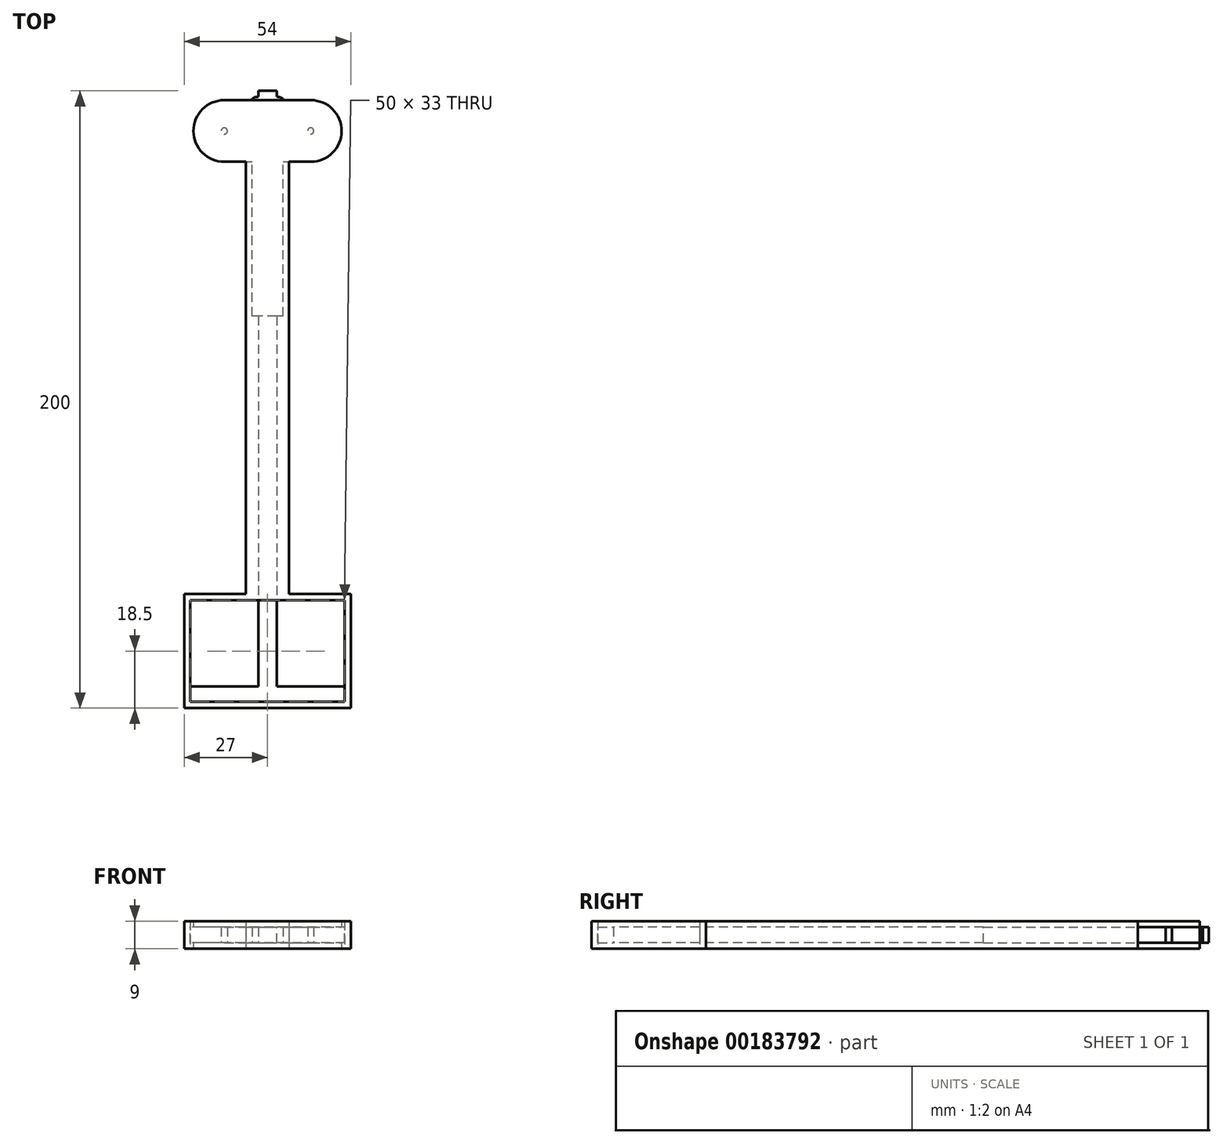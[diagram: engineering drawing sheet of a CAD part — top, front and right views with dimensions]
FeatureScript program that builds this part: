
annotation { "Feature Type Name" : "Feature", "Feature Type Description" : "" }
export const myFeature = defineFeature(function(context is Context, id is Id, definition is map)
    precondition{}
    {
        {
            var Q0;
            Q0=qCreatedBy(makeId("Top.planeOp"),FACE);
            var sketch = newSketch(context, id + "F0", { "sketchPlane" : qUnion([Q0])});
            skLineSegment(sketch, "E0.bottom", {"start": v(0, 13) * mm, "end": v(3, 13) * mm});
            skLineSegment(sketch, "E0.top", {"start": v(0, -180) * mm, "end": v(3, -180) * mm});
            skLineSegment(sketch, "E0.left", {"start": v(0, 13) * mm, "end": v(0, -180) * mm});
            skLineSegment(sketch, "E0.right", {"start": v(3, 13) * mm, "end": v(3, -180) * mm});
            skLineSegment(sketch, "E1", {"start": v(0, 10) * mm, "end": v(3, 10) * mm, "construction": true});
            skArc(sketch, "E2", {"start": v(3, 11.09) * mm, "mid": v(4.04, 10.94) * mm, "end": v(5, 10.5) * mm});
            skLineSegment(sketch, "E3", {"start": v(5, 10.5) * mm, "end": v(5, 10) * mm});
            skArc(sketch, "E4.MirrorCS", {"start": v(3, 8.91) * mm, "mid": v(4.04, 9.06) * mm, "end": v(5, 9.5) * mm});
            skLineSegment(sketch, "E5.MirrorCS", {"start": v(5, 9.5) * mm, "end": v(5, 10) * mm});
            skArc(sketch, "E6.1.0.0", {"start": v(3, 7.89) * mm, "mid": v(4.04, 7.74) * mm, "end": v(5, 7.3) * mm});
            skLineSegment(sketch, "E6.1.0.1", {"start": v(5, 7.3) * mm, "end": v(5, 6.8) * mm});
            skLineSegment(sketch, "E6.1.0.2", {"start": v(5, 6.3) * mm, "end": v(5, 6.8) * mm});
            skArc(sketch, "E6.1.0.3", {"start": v(3, 5.71) * mm, "mid": v(4.04, 5.86) * mm, "end": v(5, 6.3) * mm});
            skArc(sketch, "E6.2.0.0", {"start": v(3, 4.69) * mm, "mid": v(4.04, 4.54) * mm, "end": v(5, 4.1) * mm});
            skLineSegment(sketch, "E6.2.0.1", {"start": v(5, 4.1) * mm, "end": v(5, 3.6) * mm});
            skLineSegment(sketch, "E6.2.0.2", {"start": v(5, 3.1) * mm, "end": v(5, 3.6) * mm});
            skArc(sketch, "E6.2.0.3", {"start": v(3, 2.51) * mm, "mid": v(4.04, 2.66) * mm, "end": v(5, 3.1) * mm});
            skLineSegment(sketch, "E6.direction1", {"start": v(3, 7.39) * mm, "end": v(3, 4.19) * mm, "construction": true});
            skArc(sketch, "E7.0.3.0", {"start": v(3, 1.49) * mm, "mid": v(4.04, 1.34) * mm, "end": v(5, 0.9) * mm});
            skLineSegment(sketch, "E7.4.3.0", {"start": v(5, 0.9) * mm, "end": v(5, 0.4) * mm});
            skLineSegment(sketch, "E7.7.3.0", {"start": v(5, -0.1) * mm, "end": v(5, 0.4) * mm});
            skArc(sketch, "E7.10.3.0", {"start": v(3, -0.69) * mm, "mid": v(4.04, -0.54) * mm, "end": v(5, -0.1) * mm});
            skArc(sketch, "E7.0.4.0", {"start": v(3, -1.71) * mm, "mid": v(4.04, -1.86) * mm, "end": v(5, -2.3) * mm});
            skLineSegment(sketch, "E7.4.4.0", {"start": v(5, -2.3) * mm, "end": v(5, -2.8) * mm});
            skLineSegment(sketch, "E7.7.4.0", {"start": v(5, -3.3) * mm, "end": v(5, -2.8) * mm});
            skArc(sketch, "E7.10.4.0", {"start": v(3, -3.89) * mm, "mid": v(4.04, -3.74) * mm, "end": v(5, -3.3) * mm});
            skArc(sketch, "E7.0.5.0", {"start": v(3, -4.91) * mm, "mid": v(4.04, -5.06) * mm, "end": v(5, -5.5) * mm});
            skLineSegment(sketch, "E7.4.5.0", {"start": v(5, -5.5) * mm, "end": v(5, -6) * mm});
            skLineSegment(sketch, "E7.7.5.0", {"start": v(5, -6.5) * mm, "end": v(5, -6) * mm});
            skArc(sketch, "E7.10.5.0", {"start": v(3, -7.09) * mm, "mid": v(4.04, -6.94) * mm, "end": v(5, -6.5) * mm});
            skArc(sketch, "E7.0.6.0", {"start": v(3, -8.11) * mm, "mid": v(4.04, -8.26) * mm, "end": v(5, -8.7) * mm});
            skLineSegment(sketch, "E7.4.6.0", {"start": v(5, -8.7) * mm, "end": v(5, -9.2) * mm});
            skLineSegment(sketch, "E7.7.6.0", {"start": v(5, -9.7) * mm, "end": v(5, -9.2) * mm});
            skArc(sketch, "E7.10.6.0", {"start": v(3, -10.29) * mm, "mid": v(4.04, -10.14) * mm, "end": v(5, -9.7) * mm});
            skArc(sketch, "E7.0.7.0", {"start": v(3, -11.31) * mm, "mid": v(4.04, -11.46) * mm, "end": v(5, -11.9) * mm});
            skLineSegment(sketch, "E7.4.7.0", {"start": v(5, -11.9) * mm, "end": v(5, -12.4) * mm});
            skLineSegment(sketch, "E7.7.7.0", {"start": v(5, -12.9) * mm, "end": v(5, -12.4) * mm});
            skArc(sketch, "E7.10.7.0", {"start": v(3, -13.49) * mm, "mid": v(4.04, -13.34) * mm, "end": v(5, -12.9) * mm});
            skArc(sketch, "E7.0.8.0", {"start": v(3, -14.51) * mm, "mid": v(4.04, -14.66) * mm, "end": v(5, -15.1) * mm});
            skLineSegment(sketch, "E7.4.8.0", {"start": v(5, -15.1) * mm, "end": v(5, -15.6) * mm});
            skLineSegment(sketch, "E7.7.8.0", {"start": v(5, -16.1) * mm, "end": v(5, -15.6) * mm});
            skArc(sketch, "E7.10.8.0", {"start": v(3, -16.69) * mm, "mid": v(4.04, -16.54) * mm, "end": v(5, -16.1) * mm});
            skArc(sketch, "E7.0.9.0", {"start": v(3, -17.71) * mm, "mid": v(4.04, -17.86) * mm, "end": v(5, -18.3) * mm});
            skLineSegment(sketch, "E7.4.9.0", {"start": v(5, -18.3) * mm, "end": v(5, -18.8) * mm});
            skLineSegment(sketch, "E7.7.9.0", {"start": v(5, -19.3) * mm, "end": v(5, -18.8) * mm});
            skArc(sketch, "E7.10.9.0", {"start": v(3, -19.89) * mm, "mid": v(4.04, -19.74) * mm, "end": v(5, -19.3) * mm});
            skArc(sketch, "E7.0.10.0", {"start": v(3, -20.91) * mm, "mid": v(4.04, -21.06) * mm, "end": v(5, -21.5) * mm});
            skLineSegment(sketch, "E7.4.10.0", {"start": v(5, -21.5) * mm, "end": v(5, -22) * mm});
            skLineSegment(sketch, "E7.7.10.0", {"start": v(5, -22.5) * mm, "end": v(5, -22) * mm});
            skArc(sketch, "E7.10.10.0", {"start": v(3, -23.09) * mm, "mid": v(4.04, -22.94) * mm, "end": v(5, -22.5) * mm});
            skArc(sketch, "E7.0.11.0", {"start": v(3, -24.11) * mm, "mid": v(4.04, -24.26) * mm, "end": v(5, -24.7) * mm});
            skLineSegment(sketch, "E7.4.11.0", {"start": v(5, -24.7) * mm, "end": v(5, -25.2) * mm});
            skLineSegment(sketch, "E7.7.11.0", {"start": v(5, -25.7) * mm, "end": v(5, -25.2) * mm});
            skArc(sketch, "E7.10.11.0", {"start": v(3, -26.29) * mm, "mid": v(4.04, -26.14) * mm, "end": v(5, -25.7) * mm});
            skArc(sketch, "E7.0.12.0", {"start": v(3, -27.31) * mm, "mid": v(4.04, -27.46) * mm, "end": v(5, -27.9) * mm});
            skLineSegment(sketch, "E7.4.12.0", {"start": v(5, -27.9) * mm, "end": v(5, -28.4) * mm});
            skLineSegment(sketch, "E7.7.12.0", {"start": v(5, -28.9) * mm, "end": v(5, -28.4) * mm});
            skArc(sketch, "E7.10.12.0", {"start": v(3, -29.49) * mm, "mid": v(4.04, -29.34) * mm, "end": v(5, -28.9) * mm});
            skArc(sketch, "E7.0.13.0", {"start": v(3, -30.51) * mm, "mid": v(4.04, -30.66) * mm, "end": v(5, -31.1) * mm});
            skLineSegment(sketch, "E7.4.13.0", {"start": v(5, -31.1) * mm, "end": v(5, -31.6) * mm});
            skLineSegment(sketch, "E7.7.13.0", {"start": v(5, -32.1) * mm, "end": v(5, -31.6) * mm});
            skArc(sketch, "E7.10.13.0", {"start": v(3, -32.69) * mm, "mid": v(4.04, -32.54) * mm, "end": v(5, -32.1) * mm});
            skArc(sketch, "E7.0.14.0", {"start": v(3, -33.71) * mm, "mid": v(4.04, -33.86) * mm, "end": v(5, -34.3) * mm});
            skLineSegment(sketch, "E7.4.14.0", {"start": v(5, -34.3) * mm, "end": v(5, -34.8) * mm});
            skLineSegment(sketch, "E7.7.14.0", {"start": v(5, -35.3) * mm, "end": v(5, -34.8) * mm});
            skArc(sketch, "E7.10.14.0", {"start": v(3, -35.89) * mm, "mid": v(4.04, -35.74) * mm, "end": v(5, -35.3) * mm});
            skArc(sketch, "E7.0.15.0", {"start": v(3, -36.91) * mm, "mid": v(4.04, -37.06) * mm, "end": v(5, -37.5) * mm});
            skLineSegment(sketch, "E7.4.15.0", {"start": v(5, -37.5) * mm, "end": v(5, -38) * mm});
            skLineSegment(sketch, "E7.7.15.0", {"start": v(5, -38.5) * mm, "end": v(5, -38) * mm});
            skArc(sketch, "E7.10.15.0", {"start": v(3, -39.09) * mm, "mid": v(4.04, -38.94) * mm, "end": v(5, -38.5) * mm});
            skSolve(sketch);
        }
        {
            var Q0;
            Q0 = qSketchRegion(id + "F0", true);
            extrude(context, id + "F1", {"entities" : qUnion([Q0]), "depth" : 5 * mm});
        }
        {
            var Q0;
            Q0=makeQuery(id+"F1.opExtrude","SWEPT_BODY",BODY,{"disambiguationData":[OSD([sQuery(id+"F0.wireOp",EDGE,"E0.bottom"),sQuery(id+"F0.wireOp",EDGE,"E0.top"),sQuery(id+"F0.wireOp",EDGE,"E0.left"),sQuery(id+"F0.wireOp",EDGE,"E0.right"),sQuery(id+"F0.wireOp",EDGE,"E2"),sQuery(id+"F0.wireOp",EDGE,"E3"),sQuery(id+"F0.wireOp",EDGE,"E4.MirrorCS"),sQuery(id+"F0.wireOp",EDGE,"E5.MirrorCS"),sQuery(id+"F0.wireOp",EDGE,"E6.1.0.0"),sQuery(id+"F0.wireOp",EDGE,"E6.1.0.1"),sQuery(id+"F0.wireOp",EDGE,"E6.1.0.2"),sQuery(id+"F0.wireOp",EDGE,"E6.1.0.3"),sQuery(id+"F0.wireOp",EDGE,"E6.2.0.0"),sQuery(id+"F0.wireOp",EDGE,"E6.2.0.1"),sQuery(id+"F0.wireOp",EDGE,"E6.2.0.2"),sQuery(id+"F0.wireOp",EDGE,"E6.2.0.3"),sQuery(id+"F0.wireOp",EDGE,"E7.0.3.0"),sQuery(id+"F0.wireOp",EDGE,"E7.4.3.0"),sQuery(id+"F0.wireOp",EDGE,"E7.7.3.0"),sQuery(id+"F0.wireOp",EDGE,"E7.10.3.0"),sQuery(id+"F0.wireOp",EDGE,"E7.0.4.0"),sQuery(id+"F0.wireOp",EDGE,"E7.4.4.0"),sQuery(id+"F0.wireOp",EDGE,"E7.7.4.0"),sQuery(id+"F0.wireOp",EDGE,"E7.10.4.0"),sQuery(id+"F0.wireOp",EDGE,"E7.0.5.0"),sQuery(id+"F0.wireOp",EDGE,"E7.4.5.0"),sQuery(id+"F0.wireOp",EDGE,"E7.7.5.0"),sQuery(id+"F0.wireOp",EDGE,"E7.10.5.0"),sQuery(id+"F0.wireOp",EDGE,"E7.0.6.0"),sQuery(id+"F0.wireOp",EDGE,"E7.4.6.0"),sQuery(id+"F0.wireOp",EDGE,"E7.7.6.0"),sQuery(id+"F0.wireOp",EDGE,"E7.10.6.0"),sQuery(id+"F0.wireOp",EDGE,"E7.0.7.0"),sQuery(id+"F0.wireOp",EDGE,"E7.4.7.0"),sQuery(id+"F0.wireOp",EDGE,"E7.7.7.0"),sQuery(id+"F0.wireOp",EDGE,"E7.10.7.0"),sQuery(id+"F0.wireOp",EDGE,"E7.0.8.0"),sQuery(id+"F0.wireOp",EDGE,"E7.4.8.0"),sQuery(id+"F0.wireOp",EDGE,"E7.7.8.0"),sQuery(id+"F0.wireOp",EDGE,"E7.10.8.0"),sQuery(id+"F0.wireOp",EDGE,"E7.0.9.0"),sQuery(id+"F0.wireOp",EDGE,"E7.4.9.0"),sQuery(id+"F0.wireOp",EDGE,"E7.7.9.0"),sQuery(id+"F0.wireOp",EDGE,"E7.10.9.0"),sQuery(id+"F0.wireOp",EDGE,"E7.0.10.0"),sQuery(id+"F0.wireOp",EDGE,"E7.4.10.0"),sQuery(id+"F0.wireOp",EDGE,"E7.7.10.0"),sQuery(id+"F0.wireOp",EDGE,"E7.10.10.0"),sQuery(id+"F0.wireOp",EDGE,"E7.0.11.0"),sQuery(id+"F0.wireOp",EDGE,"E7.4.11.0"),sQuery(id+"F0.wireOp",EDGE,"E7.7.11.0"),sQuery(id+"F0.wireOp",EDGE,"E7.10.11.0"),sQuery(id+"F0.wireOp",EDGE,"E7.0.12.0"),sQuery(id+"F0.wireOp",EDGE,"E7.4.12.0"),sQuery(id+"F0.wireOp",EDGE,"E7.7.12.0"),sQuery(id+"F0.wireOp",EDGE,"E7.10.12.0"),sQuery(id+"F0.wireOp",EDGE,"E7.0.13.0"),sQuery(id+"F0.wireOp",EDGE,"E7.4.13.0"),sQuery(id+"F0.wireOp",EDGE,"E7.7.13.0"),sQuery(id+"F0.wireOp",EDGE,"E7.10.13.0"),sQuery(id+"F0.wireOp",EDGE,"E7.0.14.0"),sQuery(id+"F0.wireOp",EDGE,"E7.4.14.0"),sQuery(id+"F0.wireOp",EDGE,"E7.7.14.0"),sQuery(id+"F0.wireOp",EDGE,"E7.10.14.0"),sQuery(id+"F0.wireOp",EDGE,"E7.0.15.0"),sQuery(id+"F0.wireOp",EDGE,"E7.4.15.0"),sQuery(id+"F0.wireOp",EDGE,"E7.7.15.0"),sQuery(id+"F0.wireOp",EDGE,"E7.10.15.0")])]});
            var Q1;
            Q1=makeQuery(id+"F1.opExtrude","SWEPT_FACE",FACE,{"disambiguationData":[OSD([sQuery(id+"F0.wireOp",EDGE,"E0.left")])]});
            mirror(context, id + "F2", {"operationType" : NewBodyOperationType.ADD, "entities" : qUnion([Q0]), "mirrorPlane" : qUnion([Q1])});
        }
        {
            var Q0;
            {var subQ0=makeQuery(id+"F1.opExtrude","SWEPT_FACE",FACE,{"disambiguationData":[OSD([sQuery(id+"F0.wireOp",EDGE,"E0.top")])]});Q0=makeQuery(id+"F2.boolean.opBoolean","MERGE",FACE,{"derivedFrom":[subQ0,makeQuery(id+"F2.opPattern","COPY",FACE,{"derivedFrom":subQ0,"instanceName":"1"})]});}
            var sketch = newSketch(context, id + "F3", { "sketchPlane" : qUnion([Q0])});
            skLineSegment(sketch, "E8.bottom", {"start": v(25, 0) * mm, "end": v(-25, 0) * mm});
            skLineSegment(sketch, "E8.top", {"start": v(25, 5) * mm, "end": v(-25, 5) * mm});
            skLineSegment(sketch, "E8.left", {"start": v(25, 0) * mm, "end": v(25, 5) * mm});
            skLineSegment(sketch, "E8.right", {"start": v(-25, 0) * mm, "end": v(-25, 5) * mm});
            skPoint(sketch, "E8.middle", {"position": v(0, 2.5) * mm});
            skPoint(sketch, "E8.middle.positionSnap0", {"position": v(3, 2.5) * mm});
            skPoint(sketch, "E8.centerSnap0", {"position": v(3, 2.5) * mm});
            skSolve(sketch);
        }
        {
            var Q0;
            Q0 = qSketchRegion(id + "F3", true);
            extrude(context, id + "F4", {"entities" : qUnion([Q0]), "operationType" : NewBodyOperationType.ADD, "depth" : 5 * mm});
        }
        {
            var Q0;
            Q0=qCreatedBy(makeId("Top.planeOp"),FACE);
            var sketch = newSketch(context, id + "F5", { "sketchPlane" : qUnion([Q0])});
            skCircle(sketch, "E9", {"center": v(14, 0) * mm, "radius": 10 * mm});
            skLineSegment(sketch, "E10", {"start": v(0, 10) * mm, "end": v(14, 10) * mm});
            skLineSegment(sketch, "E11", {"start": v(14, -10) * mm, "end": v(7, -10) * mm});
            skLineSegment(sketch, "E12", {"start": v(7, -10) * mm, "end": v(7, -150) * mm});
            skLineSegment(sketch, "E13", {"start": v(7, -150) * mm, "end": v(27, -150) * mm});
            skLineSegment(sketch, "E14", {"start": v(27, -150) * mm, "end": v(27, -187) * mm});
            skLineSegment(sketch, "E15", {"start": v(27, -187) * mm, "end": v(0, -187) * mm});
            skLineSegment(sketch, "E16.MirrorCS", {"start": v(0, 10) * mm, "end": v(-14, 10) * mm});
            skCircle(sketch, "E17.MirrorC", {"center": v(-14, 0) * mm, "radius": 10 * mm});
            skLineSegment(sketch, "E18.MirrorCS", {"start": v(-14, -10) * mm, "end": v(-7, -10) * mm});
            skLineSegment(sketch, "E19.MirrorCS", {"start": v(-7, -10) * mm, "end": v(-7, -150) * mm});
            skLineSegment(sketch, "E20.MirrorCS", {"start": v(-7, -150) * mm, "end": v(-27, -150) * mm});
            skLineSegment(sketch, "E21.MirrorCS", {"start": v(-27, -150) * mm, "end": v(-27, -187) * mm});
            skLineSegment(sketch, "E22.MirrorCS", {"start": v(-27, -187) * mm, "end": v(0, -187) * mm});
            skLineSegment(sketch, "E23.bottom", {"start": v(-25, -185) * mm, "end": v(25, -185) * mm});
            skLineSegment(sketch, "E23.top", {"start": v(-25, -152) * mm, "end": v(25, -152) * mm});
            skLineSegment(sketch, "E23.left", {"start": v(-25, -185) * mm, "end": v(-25, -152) * mm});
            skLineSegment(sketch, "E23.right", {"start": v(25, -185) * mm, "end": v(25, -152) * mm});
            skPoint(sketch, "E23.middle", {"position": v(0, -168.5) * mm});
            skSolve(sketch);
        }
        {
            var Q0;
            Q0 = qSketchRegion(id + "F5", true);
            extrude(context, id + "F6", {"entities" : qUnion([Q0]), "depth" : 7 * mm, "hasSecondDirection" : true, "secondDirectionOppositeDirection" : true, "secondDirectionDepth" : 2 * mm});
        }
        {
            var Q0;
            Q0=makeQuery(id+"F1.opExtrude","SWEPT_BODY",BODY,{"disambiguationData":[OSD([sQuery(id+"F0.wireOp",EDGE,"E0.bottom"),sQuery(id+"F0.wireOp",EDGE,"E0.top"),sQuery(id+"F0.wireOp",EDGE,"E0.left"),sQuery(id+"F0.wireOp",EDGE,"E0.right"),sQuery(id+"F0.wireOp",EDGE,"E2"),sQuery(id+"F0.wireOp",EDGE,"E3"),sQuery(id+"F0.wireOp",EDGE,"E4.MirrorCS"),sQuery(id+"F0.wireOp",EDGE,"E5.MirrorCS"),sQuery(id+"F0.wireOp",EDGE,"E6.1.0.0"),sQuery(id+"F0.wireOp",EDGE,"E6.1.0.1"),sQuery(id+"F0.wireOp",EDGE,"E6.1.0.2"),sQuery(id+"F0.wireOp",EDGE,"E6.1.0.3"),sQuery(id+"F0.wireOp",EDGE,"E6.2.0.0"),sQuery(id+"F0.wireOp",EDGE,"E6.2.0.1"),sQuery(id+"F0.wireOp",EDGE,"E6.2.0.2"),sQuery(id+"F0.wireOp",EDGE,"E6.2.0.3"),sQuery(id+"F0.wireOp",EDGE,"E7.0.3.0"),sQuery(id+"F0.wireOp",EDGE,"E7.4.3.0"),sQuery(id+"F0.wireOp",EDGE,"E7.7.3.0"),sQuery(id+"F0.wireOp",EDGE,"E7.10.3.0"),sQuery(id+"F0.wireOp",EDGE,"E7.0.4.0"),sQuery(id+"F0.wireOp",EDGE,"E7.4.4.0"),sQuery(id+"F0.wireOp",EDGE,"E7.7.4.0"),sQuery(id+"F0.wireOp",EDGE,"E7.10.4.0"),sQuery(id+"F0.wireOp",EDGE,"E7.0.5.0"),sQuery(id+"F0.wireOp",EDGE,"E7.4.5.0"),sQuery(id+"F0.wireOp",EDGE,"E7.7.5.0"),sQuery(id+"F0.wireOp",EDGE,"E7.10.5.0"),sQuery(id+"F0.wireOp",EDGE,"E7.0.6.0"),sQuery(id+"F0.wireOp",EDGE,"E7.4.6.0"),sQuery(id+"F0.wireOp",EDGE,"E7.7.6.0"),sQuery(id+"F0.wireOp",EDGE,"E7.10.6.0"),sQuery(id+"F0.wireOp",EDGE,"E7.0.7.0"),sQuery(id+"F0.wireOp",EDGE,"E7.4.7.0"),sQuery(id+"F0.wireOp",EDGE,"E7.7.7.0"),sQuery(id+"F0.wireOp",EDGE,"E7.10.7.0"),sQuery(id+"F0.wireOp",EDGE,"E7.0.8.0"),sQuery(id+"F0.wireOp",EDGE,"E7.4.8.0"),sQuery(id+"F0.wireOp",EDGE,"E7.7.8.0"),sQuery(id+"F0.wireOp",EDGE,"E7.10.8.0"),sQuery(id+"F0.wireOp",EDGE,"E7.0.9.0"),sQuery(id+"F0.wireOp",EDGE,"E7.4.9.0"),sQuery(id+"F0.wireOp",EDGE,"E7.7.9.0"),sQuery(id+"F0.wireOp",EDGE,"E7.10.9.0"),sQuery(id+"F0.wireOp",EDGE,"E7.0.10.0"),sQuery(id+"F0.wireOp",EDGE,"E7.4.10.0"),sQuery(id+"F0.wireOp",EDGE,"E7.7.10.0"),sQuery(id+"F0.wireOp",EDGE,"E7.10.10.0"),sQuery(id+"F0.wireOp",EDGE,"E7.0.11.0"),sQuery(id+"F0.wireOp",EDGE,"E7.4.11.0"),sQuery(id+"F0.wireOp",EDGE,"E7.7.11.0"),sQuery(id+"F0.wireOp",EDGE,"E7.10.11.0"),sQuery(id+"F0.wireOp",EDGE,"E7.0.12.0"),sQuery(id+"F0.wireOp",EDGE,"E7.4.12.0"),sQuery(id+"F0.wireOp",EDGE,"E7.7.12.0"),sQuery(id+"F0.wireOp",EDGE,"E7.10.12.0"),sQuery(id+"F0.wireOp",EDGE,"E7.0.13.0"),sQuery(id+"F0.wireOp",EDGE,"E7.4.13.0"),sQuery(id+"F0.wireOp",EDGE,"E7.7.13.0"),sQuery(id+"F0.wireOp",EDGE,"E7.10.13.0"),sQuery(id+"F0.wireOp",EDGE,"E7.0.14.0"),sQuery(id+"F0.wireOp",EDGE,"E7.4.14.0"),sQuery(id+"F0.wireOp",EDGE,"E7.7.14.0"),sQuery(id+"F0.wireOp",EDGE,"E7.10.14.0"),sQuery(id+"F0.wireOp",EDGE,"E7.0.15.0"),sQuery(id+"F0.wireOp",EDGE,"E7.4.15.0"),sQuery(id+"F0.wireOp",EDGE,"E7.7.15.0"),sQuery(id+"F0.wireOp",EDGE,"E7.10.15.0")])]});
            var Q1;
            Q1=makeQuery(id+"F6.opExtrude","SWEPT_BODY",BODY,{"disambiguationData":[OSD([sQuery(id+"F5.wireOp",EDGE,"E9"),sQuery(id+"F5.wireOp",EDGE,"E10"),sQuery(id+"F5.wireOp",EDGE,"E11"),sQuery(id+"F5.wireOp",EDGE,"E12"),sQuery(id+"F5.wireOp",EDGE,"E13"),sQuery(id+"F5.wireOp",EDGE,"E14"),sQuery(id+"F5.wireOp",EDGE,"E15"),sQuery(id+"F5.wireOp",EDGE,"E16.MirrorCS"),sQuery(id+"F5.wireOp",EDGE,"E17.MirrorC"),sQuery(id+"F5.wireOp",EDGE,"E18.MirrorCS"),sQuery(id+"F5.wireOp",EDGE,"E19.MirrorCS"),sQuery(id+"F5.wireOp",EDGE,"E20.MirrorCS"),sQuery(id+"F5.wireOp",EDGE,"E21.MirrorCS"),sQuery(id+"F5.wireOp",EDGE,"E22.MirrorCS"),sQuery(id+"F5.wireOp",EDGE,"E23.bottom"),sQuery(id+"F5.wireOp",EDGE,"E23.top"),sQuery(id+"F5.wireOp",EDGE,"E23.left"),sQuery(id+"F5.wireOp",EDGE,"E23.right")])]});
            booleanBodies(context, id + "F7", {"operationType" : BooleanOperationType.SUBTRACTION, "tools" : qUnion([Q0]), "targets" : qUnion([Q1]), "keepTools" : true});
        }
        {
            var Q0;
            Q0=qCreatedBy(makeId("Top.planeOp"),FACE);
            var sketch = newSketch(context, id + "F8", { "sketchPlane" : qUnion([Q0])});
            skArc(sketch, "E24.0", {"start": v(-14, -10) * mm, "mid": v(-24, 0) * mm, "end": v(-14, 10) * mm});
            skArc(sketch, "E25.0", {"start": v(14, -10) * mm, "mid": v(24, 0) * mm, "end": v(14, 10) * mm});
            skLineSegment(sketch, "E26.0", {"start": v(-14, 10) * mm, "end": v(14, 10) * mm});
            skLineSegment(sketch, "E27", {"start": v(-14, -10) * mm, "end": v(14, -10) * mm});
            skSolve(sketch);
        }
        {
            var Q0;
            Q0 = qSketchRegion(id + "F8", true);
            extrude(context, id + "F9", {"entities" : qUnion([Q0]), "operationType" : NewBodyOperationType.REMOVE, "depth" : 5 * mm});
        }
        {
            var Q0;
            {var subQ3=sQuery(id+"F8.wireOp",EDGE,"E27");Q0=makeQuery(id+"F9.boolean.opBoolean","COPY",FACE,{"disambiguationData":[TD([makeQuery(id+"F6.opExtrude","SWEPT_FACE",FACE,{"disambiguationData":[OSD([sQuery(id+"F5.wireOp",EDGE,"E18.MirrorCS")])]})])],"derivedFrom":makeQuery(id+"F9.opExtrude","SWEPT_FACE",FACE,{"disambiguationData":[OSD([subQ3])]})});}
            var sketch = newSketch(context, id + "F10", { "sketchPlane" : qUnion([Q0])});
            skLineSegment(sketch, "E28.bottom", {"start": v(-5, 5) * mm, "end": v(5, 5) * mm});
            skLineSegment(sketch, "E28.top", {"start": v(-5, 0) * mm, "end": v(5, 0) * mm});
            skLineSegment(sketch, "E28.left", {"start": v(-5, 5) * mm, "end": v(-5, 0) * mm});
            skLineSegment(sketch, "E28.right", {"start": v(5, 5) * mm, "end": v(5, 0) * mm});
            skSolve(sketch);
        }
        {
            var Q0;
            Q0 = qSketchRegion(id + "F10", true);
            extrude(context, id + "F11", {"entities" : qUnion([Q0]), "operationType" : NewBodyOperationType.REMOVE, "oppositeDirection" : true, "depth" : 50 * mm});
        }
        {
            var Q0;
            Q0=qCreatedBy(makeId("Top.planeOp"),FACE);
            var sketch = newSketch(context, id + "F12", { "sketchPlane" : qUnion([Q0])});
            skCircle(sketch, "E29", {"center": v(14, 0) * mm, "radius": 1 * mm});
            skCircle(sketch, "E30", {"center": v(-14, 0) * mm, "radius": 1 * mm});
            skSolve(sketch);
        }
        {
            var Q0;
            Q0 = qSketchRegion(id + "F12", true);
            extrude(context, id + "F13", {"entities" : qUnion([Q0]), "operationType" : NewBodyOperationType.ADD, "endBound" : BoundingType.UP_TO_NEXT, "depth" : 25 * mm});
        }
    });
